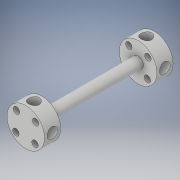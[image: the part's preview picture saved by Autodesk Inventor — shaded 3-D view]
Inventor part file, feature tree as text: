
AUTODESK INVENTOR PART (.ipt)
format: ipt  version: 2019 (Build 230136000, 136)  size: 178,176 bytes
history: native  units: in
note: dims shown in document units (in); Inventor stores cm internally (conversion verified against a paired STEP export)
features: sketch x4, extrude x2, hole x2, pattern_circular x2, plane x1, mirror x1, projected_geometry x1
ambient origin geometry x8: Origin, YZ Plane, XZ Plane, XY Plane, X Axis, Y Axis, Z Axis, Center Point
bodies: Solid1 (feature_tree)
feature tree (13):
  extrude  "Extrusion2"  Depth=0.375in TaperAngle=0.0deg
  extrude  "Extrusion3"  Depth=1.12in TaperAngle=0.0deg
  hole  "Hole2"  [1 undecoded]
  pattern_circular  "Circular Pattern2"  [2 undecoded]
  plane  "Work Plane2"
  hole  "Hole3"  [1 undecoded]
  pattern_circular  "Circular Pattern3"  Angle=45.0deg  [1 undecoded]
  mirror  "Mirror1"
  sketch  "Sketch2"  dims[d6=0.875in d7=0.375in d8=0.0in]
  sketch  "Sketch6"  dims[d17=0.25in d18=1.12in d19=0.0in]
  sketch  "Sketch7"  dims[d20=0.315in]
  projected_geometry  "Projected Loop1"
  sketch  "Sketch8"  dims[d21=0.15in d22=0.75in d23=0.375in d24=0.25in d25=0.5635in d26=1.0in d27=0.8108in d28=1.5748in d29=360.0deg d31=0.4375in d32=0.25in d33=0.75in d34=0.375in d35=0.25in d36=0.5635in d37=1.0in d38=0.8108in d39=1.5748in d40=360.0deg d42=45.0deg]
note: 5 required parameter values undecoded (feature->parameter linkage not recoverable at this tier; creation-order binding heuristic only, values carry confidence <= 0.55)
